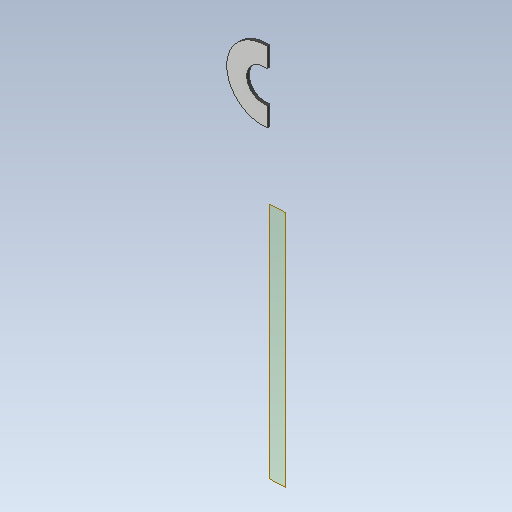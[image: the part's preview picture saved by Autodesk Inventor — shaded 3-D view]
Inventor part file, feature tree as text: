
AUTODESK INVENTOR PART (.ipt)
format: ipt  version: 2020.1 (Build 241239000, 239)  size: 118,784 bytes
history: native  units: mm
features: other x6, reference x2, plane x1, sheet_metal_op x1, sketch x1
ambient origin geometry x8: Origin, YZ Plane, XZ Plane, XY Plane, X Axis, Y Axis, Z Axis, Center Point
bodies: Solid1 (feature_tree)
feature tree (11):
  plane  "Work Plane1"
  sheet_metal_op  "Face1"
  sketch  "Sketch1"  dims[d0=30.0mm d1=6.0mm d2=4.0mm]
  reference  "Reference1"
  reference  "Reference2"
  other  "Plate1"
  other  "<path>, oppe, top.iam"
  other  "hegnspæl, oppe, top.iam"
  other  "Frame0002:1"
  other  "DIN T30 00000001:1"
  other  "<path>, oppe, top.iam"
note: 2 file-system paths scrubbed to <path> (originals preserved in map.json)
